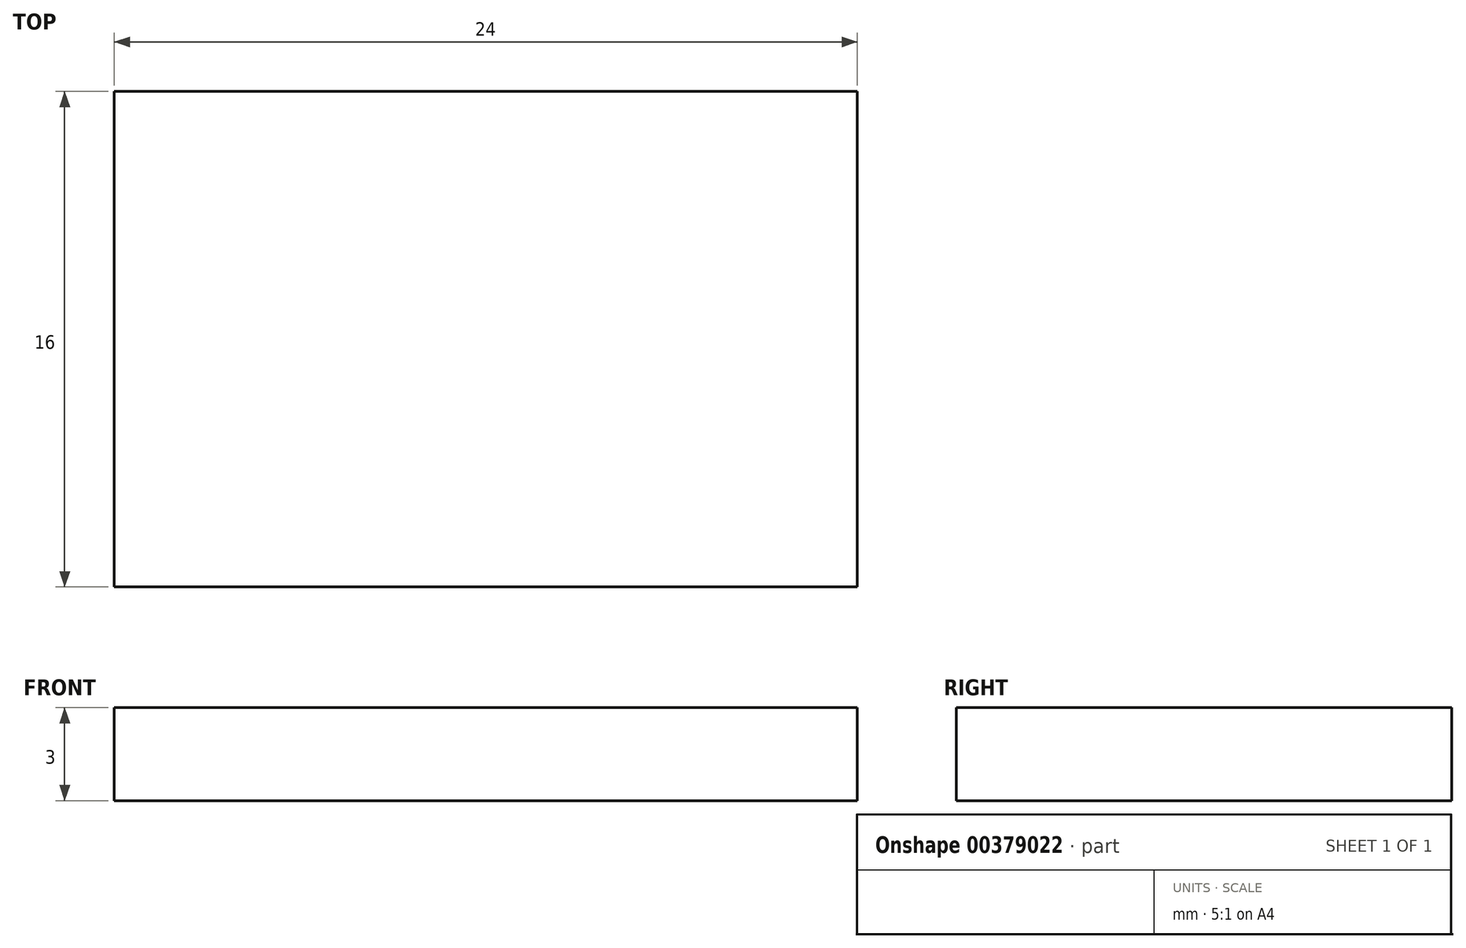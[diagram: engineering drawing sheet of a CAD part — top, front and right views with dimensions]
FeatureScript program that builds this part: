
annotation { "Feature Type Name" : "Feature", "Feature Type Description" : "" }
export const myFeature = defineFeature(function(context is Context, id is Id, definition is map)
    precondition{}
    {
        {
            var Q0;
            Q0=qCreatedBy(makeId("Top.planeOp"),FACE);
            var sketch = newSketch(context, id + "F0", { "sketchPlane" : qUnion([Q0])});
            skLineSegment(sketch, "E0.bottom", {"start": v(-12, 8) * mm, "end": v(12, 8) * mm});
            skLineSegment(sketch, "E0.top", {"start": v(-12, -8) * mm, "end": v(12, -8) * mm});
            skLineSegment(sketch, "E0.left", {"start": v(-12, 8) * mm, "end": v(-12, -8) * mm});
            skLineSegment(sketch, "E0.right", {"start": v(12, 8) * mm, "end": v(12, -8) * mm});
            skPoint(sketch, "E0.middle", {"position": v(0, 0) * mm});
            skSolve(sketch);
        }
        {
            var Q0;
            Q0=makeQuery(id+"F0.imprint","IMPRINT",FACE,{"disambiguationData":[TD([[makeQuery(id+"F0.imprint","IMPRINT",EDGE,{"derivedFrom":sQuery(id+"F0.wireOp",EDGE,"E0.bottom")}),-1.0]])]});
            extrude(context, id + "F1", {"entities" : qUnion([Q0]), "depth" : 3 * mm});
        }
    });
